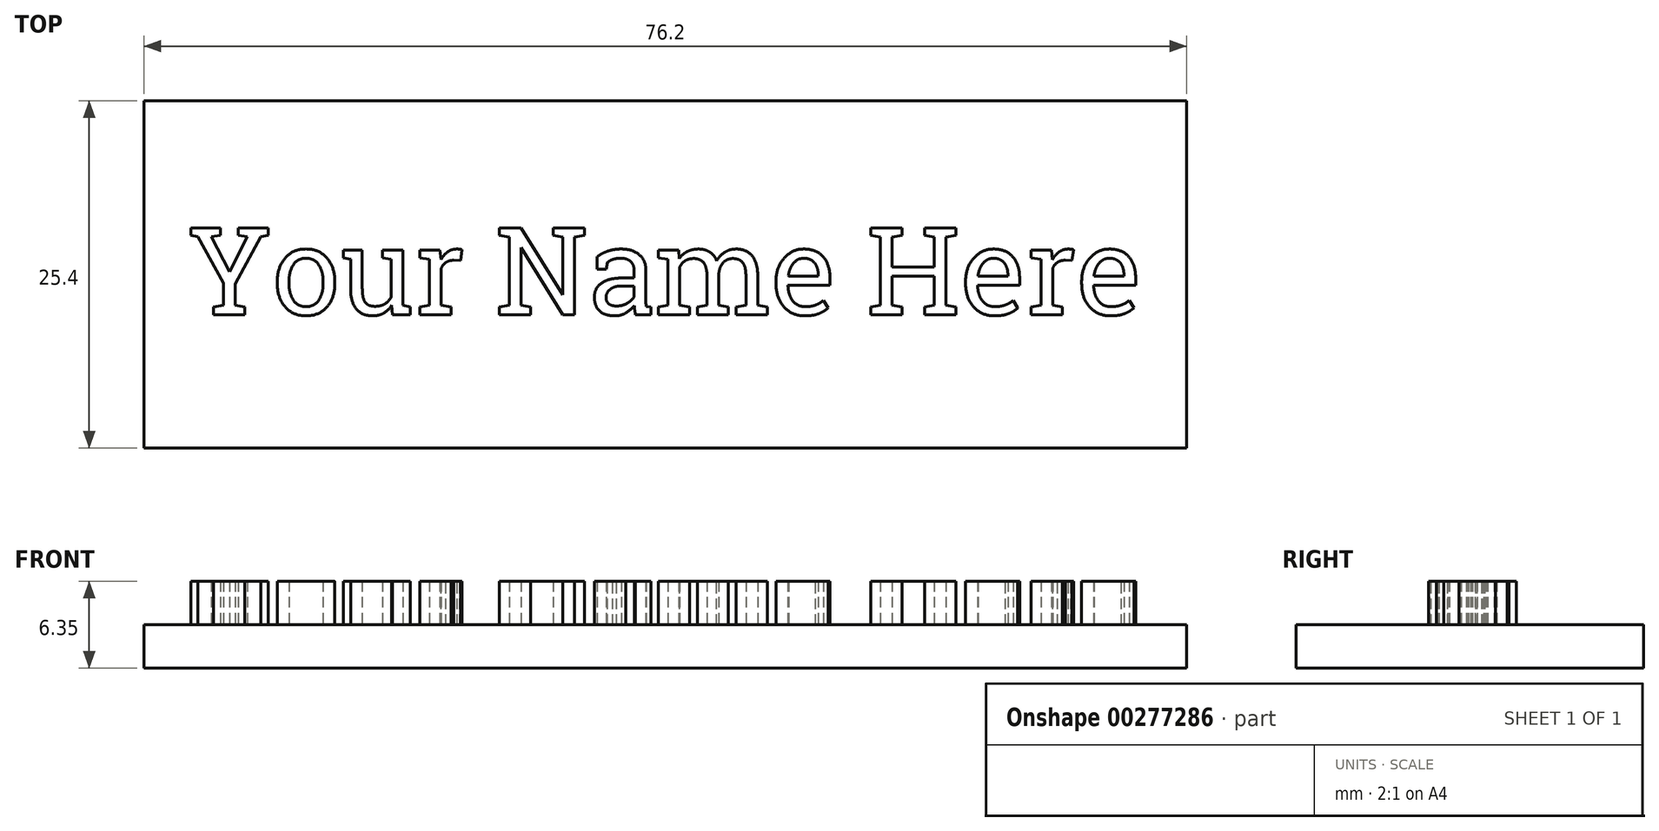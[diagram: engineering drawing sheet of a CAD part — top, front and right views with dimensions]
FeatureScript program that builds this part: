
annotation { "Feature Type Name" : "Feature", "Feature Type Description" : "" }
export const myFeature = defineFeature(function(context is Context, id is Id, definition is map)
    precondition{}
    {
        {
            var Q0;
            Q0=qCreatedBy(makeId("Top.planeOp"),FACE);
            var sketch = newSketch(context, id + "F0", { "sketchPlane" : qUnion([Q0])});
            skLineSegment(sketch, "E0.bottom", {"start": v(38.1, -12.7) * mm, "end": v(-38.1, -12.7) * mm});
            skLineSegment(sketch, "E0.top", {"start": v(38.1, 12.7) * mm, "end": v(-38.1, 12.7) * mm});
            skLineSegment(sketch, "E0.left", {"start": v(38.1, -12.7) * mm, "end": v(38.1, 12.7) * mm});
            skLineSegment(sketch, "E0.right", {"start": v(-38.1, -12.7) * mm, "end": v(-38.1, 12.7) * mm});
            skPoint(sketch, "E0.middle", {"position": v(0, 0) * mm});
            skSolve(sketch);
        }
        {
            var Q0;
            Q0=makeQuery(id+"F0.imprint","IMPRINT",FACE,{"disambiguationData":[TD([[makeQuery(id+"F0.imprint","IMPRINT",EDGE,{"derivedFrom":sQuery(id+"F0.wireOp",EDGE,"E0.bottom")}),-1.0]])]});
            extrude(context, id + "F1", {"entities" : qUnion([Q0]), "depth" : 3.17 * mm});
        }
        {
            var Q0;
            Q0=makeQuery(id+"F1.opExtrude","CAP_FACE",FACE,{"disambiguationData":[OSD([sQuery(id+"F0.wireOp",EDGE,"E0.bottom"),sQuery(id+"F0.wireOp",EDGE,"E0.top"),sQuery(id+"F0.wireOp",EDGE,"E0.left"),sQuery(id+"F0.wireOp",EDGE,"E0.right")])],"isStart":false});
            var sketch = newSketch(context, id + "F2", { "sketchPlane" : qUnion([Q0])});
            skText(sketch, "E1", { "text": "Your Name Here\n", "fontName": "RobotoSlab-Regular.ttf"});
            const initialGuessF2  = {"E1": [-0.03492, -0.00294, 1, 0, 0.00642]};
            skSetInitialGuess(sketch, initialGuessF2);
            skSolve(sketch);
        }
        {
            var Q0;
            Q0 = qSketchRegion(id + "F2", true);
            extrude(context, id + "F3", {"entities" : qUnion([Q0]), "operationType" : NewBodyOperationType.ADD, "depth" : 3.17 * mm});
        }
    });
